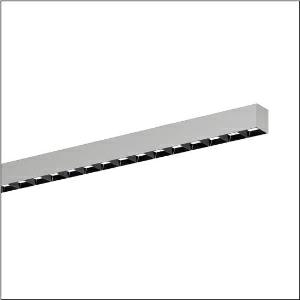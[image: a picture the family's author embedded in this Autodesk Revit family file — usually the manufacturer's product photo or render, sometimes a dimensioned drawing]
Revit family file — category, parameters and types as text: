
# Revit family: silica_21_51mx24tctas
name_source: partatom
category: Lighting Fixtures
units: mm (PartAtom-declared; Revit-internal decimal feet)

## family parameters
Cut with Voids When Loaded = No
Host = Face
Light Source = No
Part Type = Normal
Room Calculation Point = No
Round Connector Dimension = Use Diameter
Shared = No

## types (1)
- --- (1 x LED, 8200 lm, 81.1 W, 6500K)
    Apparent Load = 81 VA
    CIE Flux Codes = 74 94 99 100 100
    Color Rendering = 80
    Color Temperature = 6500K
    Default Elevation = 1800 mm
    Description = Silica 21, office luminaire, primary light control with darklight reflector, of PMMA, black, light emission: direct distribution, primary light characteristic: asymmetric, installation type: surface-mounted, LED, rated luminous flux: 8.200lm, luminous efficacy: 96lm/W, light colour: 8tw, colour temperature: 2700..6500K, control gear: DALI DT8, with terminal, 3+2-pole, max. 2.5mm², mains connection: 220..240V, AC, 50/60Hz, rated input power: 85.2W, luminaire housing, of aluminium, metallic grey (RAL 9006), length: 3.004mm, width: 53mm, height: 53mm, protection rating (complete): IP20, insulation class (complete): insulation class I (protective earthing), certification: CE, permissible operating ambient temperature: 0..+35°C, standard: EN 50419, packaging unit: 1 piece
    Height = 53 mm
    Lamp = 1 x LED
    Lamp Light Flux = 8200 lm
    Lamp Power = 81.1 W
    Lamp count = 1
    Length = 3004 mm
    Luminous efficacy = 101 lm/W
    Manufacturer = Siteco
    ModVariant = No
    Model = 51MX24TCTAS
    Mounting Place = Ceiling
    Mounting Type = Surface mounted
    Number of Poles = 1
    OnlyDefault = Yes
    Power Factor = 1
    Product Name = Silica 21
    Product group = office luminaire | ceiling mounted
    ProductGroupID = 301
    Protection Class = Protection class I
    Protection Degree = IP 20
    RLX_Detail_Level = 1
    RLX_Emergency_Light_Flux = 0 lm
    RLX_Emergency_Type = 0
    RLX_Emergency_Type_DB = No
    RlxData = <blob elided: 59981 chars, md5=87215cd7>
    Socket = socket
    Standby Power = 0 W
    System Light Flux = 8200 lm
    System Power = 81 W
    Type Comments = individual setting
    Type Image = l_1335929.jpg
    URL = http://relux.com
    VarID = @adj_141019
    Voltage = 0 V
    Weight = 0.00 kg
    Width = 53 mm

## geometry (parser evidence)
native form markers: Blend x4, Sweep x10
no freeform markers — native parametric forms only
